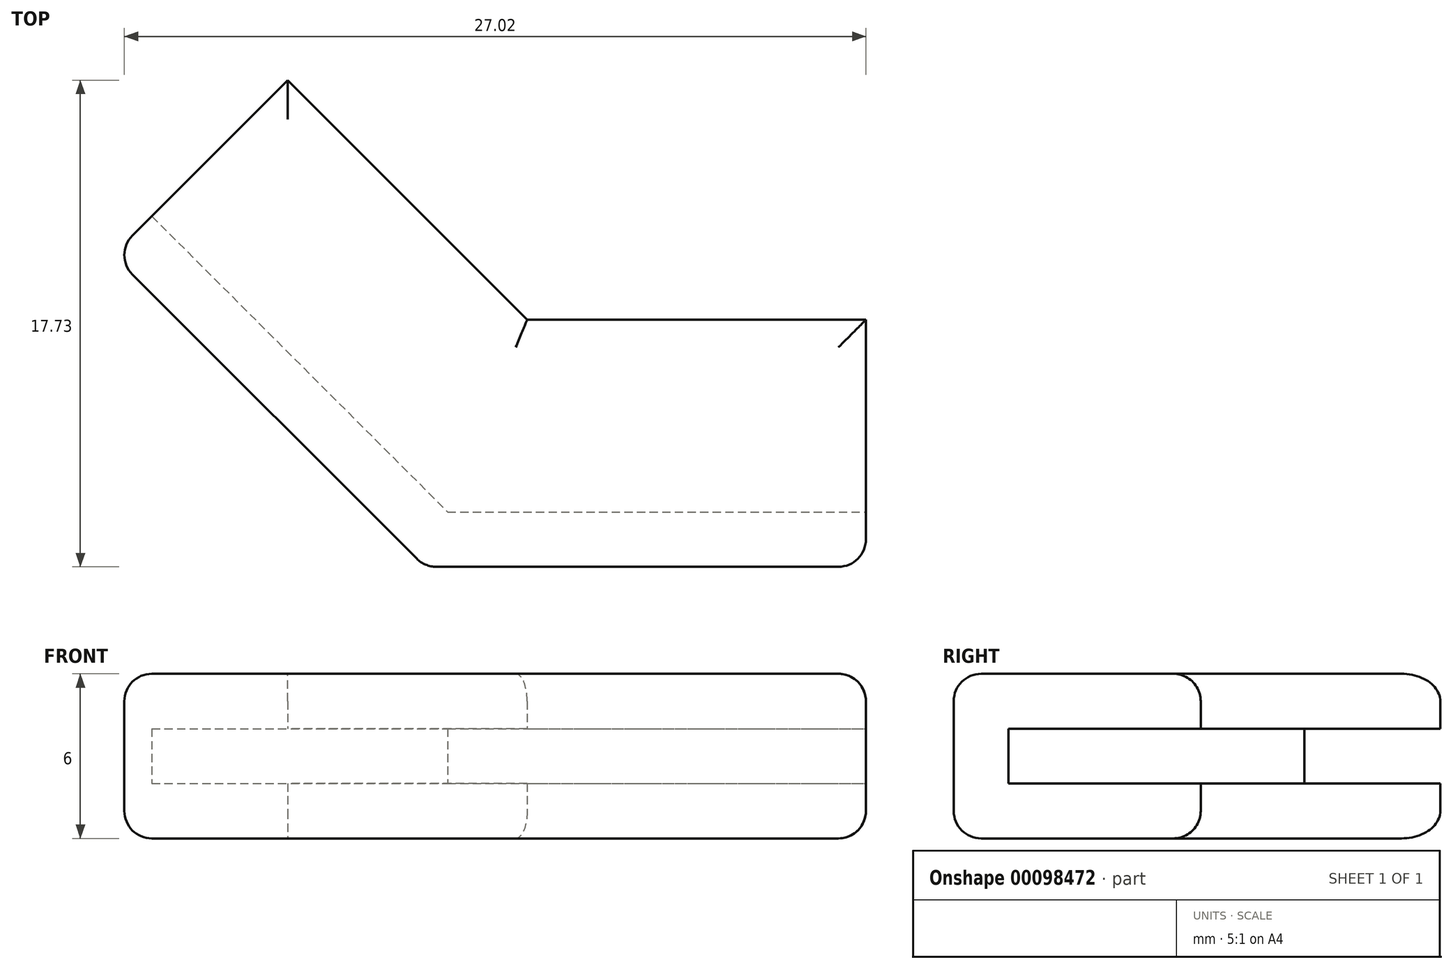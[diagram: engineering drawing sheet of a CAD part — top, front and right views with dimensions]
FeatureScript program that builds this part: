
annotation { "Feature Type Name" : "Feature", "Feature Type Description" : "" }
export const myFeature = defineFeature(function(context is Context, id is Id, definition is map)
    precondition{}
    {
        {
            var Q0;
            Q0=qCreatedBy(makeId("Top.planeOp"),FACE);
            var sketch = newSketch(context, id + "F0", { "sketchPlane" : qUnion([Q0])});
            skLineSegment(sketch, "E0", {"start": v(0, 0) * mm, "end": v(14, 0) * mm, "construction": true});
            skLineSegment(sketch, "E1", {"start": v(0, 0) * mm, "end": v(-9.9, 9.9) * mm, "construction": true});
            skLineSegment(sketch, "E2.0", {"start": v(-2.07, -5) * mm, "end": v(-13.44, 6.36) * mm});
            skLineSegment(sketch, "E2.1", {"start": v(-2.07, -5) * mm, "end": v(14, -5) * mm});
            skLineSegment(sketch, "E3.0", {"start": v(1.66, 4) * mm, "end": v(-7.07, 12.73) * mm});
            skLineSegment(sketch, "E3.1", {"start": v(1.66, 4) * mm, "end": v(14, 4) * mm});
            skLineSegment(sketch, "E4", {"start": v(-13.44, 6.36) * mm, "end": v(-7.07, 12.73) * mm});
            skLineSegment(sketch, "E5", {"start": v(14, -5) * mm, "end": v(14, 4) * mm});
            skSolve(sketch);
        }
        {
            var Q0;
            Q0 = qSketchRegion(id + "F0", true);
            extrude(context, id + "F1", {"entities" : qUnion([Q0]), "depth" : 2 * mm});
        }
        {
            var Q0;
            Q0=makeQuery(id+"F1.opExtrude","CAP_FACE",FACE,{"disambiguationData":[OSD([sQuery(id+"F0.wireOp",EDGE,"E2.0"),sQuery(id+"F0.wireOp",EDGE,"E2.1"),sQuery(id+"F0.wireOp",EDGE,"E3.0"),sQuery(id+"F0.wireOp",EDGE,"E3.1"),sQuery(id+"F0.wireOp",EDGE,"E4"),sQuery(id+"F0.wireOp",EDGE,"E5")])],"isStart":false});
            var sketch = newSketch(context, id + "F2", { "sketchPlane" : qUnion([Q0])});
            skLineSegment(sketch, "E6.0", {"start": v(-13.44, 6.36) * mm, "end": v(-12.02, 7.78) * mm});
            skLineSegment(sketch, "E6.1", {"start": v(-2.07, -5) * mm, "end": v(-13.44, 6.36) * mm});
            skLineSegment(sketch, "E6.2", {"start": v(-2.07, -5) * mm, "end": v(14, -5) * mm});
            skLineSegment(sketch, "E6.3", {"start": v(14, -5) * mm, "end": v(14, -3) * mm});
            skLineSegment(sketch, "E7", {"start": v(1.66, 4) * mm, "end": v(-2.07, -5) * mm, "construction": true});
            skLineSegment(sketch, "E8", {"start": v(-12.02, 7.78) * mm, "end": v(-1.24, -3) * mm});
            skLineSegment(sketch, "E9", {"start": v(-1.24, -3) * mm, "end": v(14, -3) * mm});
            skPoint(sketch, "E10.orphan", {"position": v(-7.07, 12.73) * mm});
            skPoint(sketch, "E11.orphan", {"position": v(14, 4) * mm});
            skSolve(sketch);
        }
        {
            var Q0;
            Q0 = qSketchRegion(id + "F2", true);
            extrude(context, id + "F3", {"entities" : qUnion([Q0]), "operationType" : NewBodyOperationType.ADD, "depth" : 2 * mm});
        }
        {
            var Q0;
            Q0=makeQuery(id+"F3.opExtrude","CAP_FACE",FACE,{"disambiguationData":[OSD([sQuery(id+"F2.wireOp",EDGE,"E6.0"),sQuery(id+"F2.wireOp",EDGE,"E6.1"),sQuery(id+"F2.wireOp",EDGE,"E6.2"),sQuery(id+"F2.wireOp",EDGE,"E6.3"),sQuery(id+"F2.wireOp",EDGE,"E8"),sQuery(id+"F2.wireOp",EDGE,"E9")])],"isStart":false});
            var sketch = newSketch(context, id + "F4", { "sketchPlane" : qUnion([Q0])});
            skLineSegment(sketch, "E12.0", {"start": v(-12.02, 7.78) * mm, "end": v(-7.07, 12.73) * mm});
            skLineSegment(sketch, "E12.1", {"start": v(1.66, 4) * mm, "end": v(-7.07, 12.73) * mm});
            skLineSegment(sketch, "E12.2", {"start": v(1.66, 4) * mm, "end": v(14, 4) * mm});
            skLineSegment(sketch, "E12.3", {"start": v(14, -3) * mm, "end": v(14, 4) * mm});
            skLineSegment(sketch, "E12.4", {"start": v(14, -5) * mm, "end": v(14, -3) * mm});
            skLineSegment(sketch, "E12.5", {"start": v(-2.07, -5) * mm, "end": v(14, -5) * mm});
            skLineSegment(sketch, "E12.6", {"start": v(-2.07, -5) * mm, "end": v(-13.44, 6.36) * mm});
            skLineSegment(sketch, "E12.7", {"start": v(-13.44, 6.36) * mm, "end": v(-12.02, 7.78) * mm});
            skSolve(sketch);
        }
        {
            var Q0;
            Q0 = qSketchRegion(id + "F4", true);
            extrude(context, id + "F5", {"entities" : qUnion([Q0]), "operationType" : NewBodyOperationType.ADD, "depth" : 2 * mm});
        }
        {
            var Q0;
            Q0=makeQuery(id+"F5.boolean.opBoolean","MERGE",FACE,{"derivedFrom":[makeQuery(id+"F3.boolean.opBoolean","MERGE",FACE,{"derivedFrom":[makeQuery(id+"F1.opExtrude","SWEPT_FACE",FACE,{"disambiguationData":[OSD([sQuery(id+"F0.wireOp",EDGE,"E2.0")])]}),makeQuery(id+"F3.opExtrude","SWEPT_FACE",FACE,{"disambiguationData":[OSD([sQuery(id+"F2.wireOp",EDGE,"E6.1")])]})]}),makeQuery(id+"F5.opExtrude","SWEPT_FACE",FACE,{"disambiguationData":[OSD([sQuery(id+"F4.wireOp",EDGE,"E12.6")])]})]});
            var Q1;
            Q1=makeQuery(id+"F5.boolean.opBoolean","MERGE",FACE,{"derivedFrom":[makeQuery(id+"F3.boolean.opBoolean","MERGE",FACE,{"derivedFrom":[makeQuery(id+"F1.opExtrude","SWEPT_FACE",FACE,{"disambiguationData":[OSD([sQuery(id+"F0.wireOp",EDGE,"E2.1")])]}),makeQuery(id+"F3.opExtrude","SWEPT_FACE",FACE,{"disambiguationData":[OSD([sQuery(id+"F2.wireOp",EDGE,"E6.2")])]})]}),makeQuery(id+"F5.opExtrude","SWEPT_FACE",FACE,{"disambiguationData":[OSD([sQuery(id+"F4.wireOp",EDGE,"E12.5")])]})]});
            var Q2;
            Q2=makeQuery(id+"F1.opExtrude","CAP_FACE",FACE,{"disambiguationData":[OSD([sQuery(id+"F0.wireOp",EDGE,"E2.0"),sQuery(id+"F0.wireOp",EDGE,"E2.1"),sQuery(id+"F0.wireOp",EDGE,"E3.0"),sQuery(id+"F0.wireOp",EDGE,"E3.1"),sQuery(id+"F0.wireOp",EDGE,"E4"),sQuery(id+"F0.wireOp",EDGE,"E5")])],"isStart":true});
            var Q3;
            Q3=makeQuery(id+"F5.opExtrude","CAP_FACE",FACE,{"disambiguationData":[OSD([sQuery(id+"F4.wireOp",EDGE,"E12.0"),sQuery(id+"F4.wireOp",EDGE,"E12.1"),sQuery(id+"F4.wireOp",EDGE,"E12.2"),sQuery(id+"F4.wireOp",EDGE,"E12.3"),sQuery(id+"F4.wireOp",EDGE,"E12.4"),sQuery(id+"F4.wireOp",EDGE,"E12.5"),sQuery(id+"F4.wireOp",EDGE,"E12.6"),sQuery(id+"F4.wireOp",EDGE,"E12.7")])],"isStart":false});
            fillet(context, id + "F6", {"entities" : qUnion([Q0, Q1, Q2, Q3]), "radius" : 1 * mm, "tangentPropagation" : true, "allowEdgeOverflow" : false});
        }
    });
